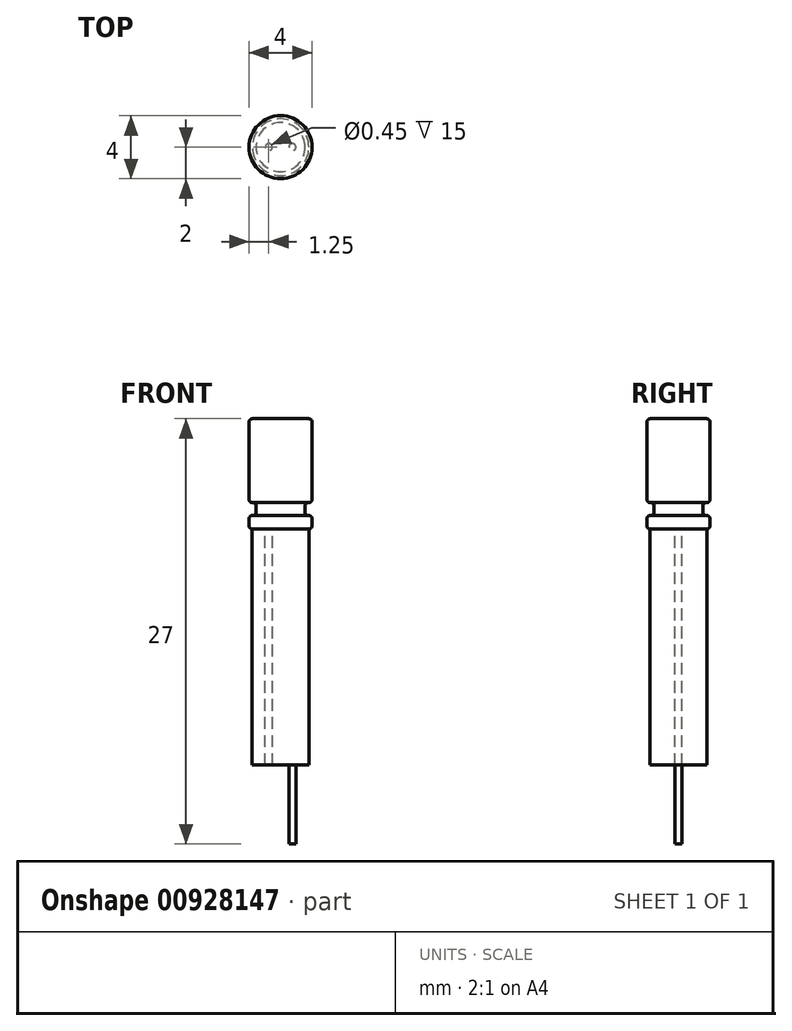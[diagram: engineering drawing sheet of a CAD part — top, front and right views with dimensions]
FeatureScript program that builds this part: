
annotation { "Feature Type Name" : "Feature", "Feature Type Description" : "" }
export const myFeature = defineFeature(function(context is Context, id is Id, definition is map)
    precondition{}
    {
        {
            var Q0;
            Q0=qCreatedBy(makeId("Top.planeOp"),FACE);
            var sketch = newSketch(context, id + "F0", { "sketchPlane" : qUnion([Q0])});
            skCircle(sketch, "E0", {"center": v(0, 0) * mm, "radius": 2 * mm});
            skSolve(sketch);
        }
        {
            var Q0;
            Q0=makeQuery(id+"F0.imprint","IMPRINT",FACE,{"disambiguationData":[TD([[makeQuery(id+"F0.imprint","IMPRINT",EDGE,{"derivedFrom":sQuery(id+"F0.wireOp",EDGE,"E0")}),1.0]])]});
            extrude(context, id + "F1", {"entities" : qUnion([Q0]), "depth" : 7 * mm, "offsetDistance" : 25 * mm});
        }
        {
            var Q0;
            Q0=qCreatedBy(makeId("Front.planeOp"),FACE);
            var sketch = newSketch(context, id + "F2", { "sketchPlane" : qUnion([Q0])});
            skLineSegment(sketch, "E1.bottom", {"start": v(2.75, 0.85) * mm, "end": v(1.56, 0.85) * mm});
            skLineSegment(sketch, "E1.top", {"start": v(2.75, 1.67) * mm, "end": v(1.56, 1.67) * mm});
            skLineSegment(sketch, "E1.left", {"start": v(2.75, 0.85) * mm, "end": v(2.75, 1.67) * mm});
            skLineSegment(sketch, "E1.right", {"start": v(1.56, 0.85) * mm, "end": v(1.56, 1.67) * mm});
            skSolve(sketch);
        }
        {
            var Q0;
            Q0=makeQuery(id+"F2.imprint","IMPRINT",FACE,{"disambiguationData":[TD([[makeQuery(id+"F2.imprint","IMPRINT",EDGE,{"derivedFrom":sQuery(id+"F2.wireOp",EDGE,"E1.bottom")}),-1.0]])]});
            var Q1;
            Q1=makeQuery(id+"F1.opExtrude","SWEPT_FACE",FACE,{"disambiguationData":[OSD([sQuery(id+"F0.wireOp",EDGE,"E0")])]});
            revolve(context, id + "F3", {"operationType" : NewBodyOperationType.REMOVE, "surfaceOperationType" : NewSurfaceOperationType.NEW, "entities" : qUnion([Q0]), "axis" : qUnion([Q1]), "revolveType" : RevolveType.FULL, "oppositeDirection" : true});
        }
        {
            var Q0;
            Q0=makeQuery(id+"F1.opExtrude","CAP_EDGE",EDGE,{"disambiguationData":[OSD([sQuery(id+"F0.wireOp",EDGE,"E0")])],"isStart":false});
            var Q1;
            Q1=makeQuery(id+"F3.boolean.opBoolean","INTERSECT",EDGE,{"derivedFrom":[makeQuery(id+"F1.opExtrude","SWEPT_FACE",FACE,{"disambiguationData":[OSD([sQuery(id+"F0.wireOp",EDGE,"E0")])]}),makeQuery(id+"F3.opRevolve","SWEPT_FACE",FACE,{"disambiguationData":[OSD([sQuery(id+"F2.wireOp",EDGE,"E1.top")])]})]});
            var Q2;
            Q2=makeQuery(id+"F3.boolean.opBoolean","COPY",EDGE,{"derivedFrom":makeQuery(id+"F3.opRevolve","SWEPT_EDGE",EDGE,{"disambiguationData":[OSD([sQuery(id+"F2.wireOp",EDGE,"E1.top"),sQuery(id+"F2.wireOp",EDGE,"E1.right")])]})});
            var Q3;
            Q3=makeQuery(id+"F3.boolean.opBoolean","INTERSECT",EDGE,{"derivedFrom":[makeQuery(id+"F1.opExtrude","SWEPT_FACE",FACE,{"disambiguationData":[OSD([sQuery(id+"F0.wireOp",EDGE,"E0")])]}),makeQuery(id+"F3.opRevolve","SWEPT_FACE",FACE,{"disambiguationData":[OSD([sQuery(id+"F2.wireOp",EDGE,"E1.bottom")])]})]});
            var Q4;
            Q4=makeQuery(id+"F1.opExtrude","CAP_EDGE",EDGE,{"disambiguationData":[OSD([sQuery(id+"F0.wireOp",EDGE,"E0")])],"isStart":true});
            var Q5;
            Q5=makeQuery(id+"F3.boolean.opBoolean","COPY",EDGE,{"derivedFrom":makeQuery(id+"F3.opRevolve","SWEPT_EDGE",EDGE,{"disambiguationData":[OSD([sQuery(id+"F2.wireOp",EDGE,"E1.bottom"),sQuery(id+"F2.wireOp",EDGE,"E1.right")])]})});
            fillet(context, id + "F4", {"entities" : qUnion([Q0, Q1, Q2, Q3, Q4, Q5]), "radius" : 0.2 * mm, "tangentPropagation" : true, "allowEdgeOverflow" : false});
        }
        {
            var Q0;
            Q0=makeQuery(id+"F1.opExtrude","CAP_FACE",FACE,{"disambiguationData":[OSD([sQuery(id+"F0.wireOp",EDGE,"E0")])],"isStart":true});
            var sketch = newSketch(context, id + "F5", { "sketchPlane" : qUnion([Q0])});
            skLineSegment(sketch, "E2", {"start": v(0, 0) * mm, "end": v(0.75, 0) * mm});
            skLineSegment(sketch, "E3", {"start": v(0.75, 0) * mm, "end": v(-0.75, 0) * mm});
            skCircle(sketch, "E4", {"center": v(0.75, 0) * mm, "radius": 0.23 * mm});
            skCircle(sketch, "E5.MirrorC", {"center": v(-0.75, 0) * mm, "radius": 0.23 * mm});
            skSolve(sketch);
        }
        {
            var Q0;
            Q0=makeQuery(id+"F5.imprint","IMPRINT",FACE,{"disambiguationData":[TD([[makeQuery(id+"F5.imprint","IMPRINT",EDGE,{"derivedFrom":sQuery(id+"F5.wireOp",EDGE,"E5.MirrorC")}),-1.0]])]});
            extrude(context, id + "F6", {"entities" : qUnion([Q0]), "operationType" : NewBodyOperationType.ADD, "depth" : 15 * mm, "offsetDistance" : 25 * mm});
        }
        {
            var Q0;
            Q0=makeQuery(id+"F5.imprint","IMPRINT",FACE,{"disambiguationData":[TD([[makeQuery(id+"F5.imprint","IMPRINT",EDGE,{"derivedFrom":sQuery(id+"F5.wireOp",EDGE,"E4")}),1.0]])]});
            extrude(context, id + "F7", {"entities" : qUnion([Q0]), "operationType" : NewBodyOperationType.ADD, "depth" : 20 * mm, "offsetDistance" : 25 * mm});
        }
    });
